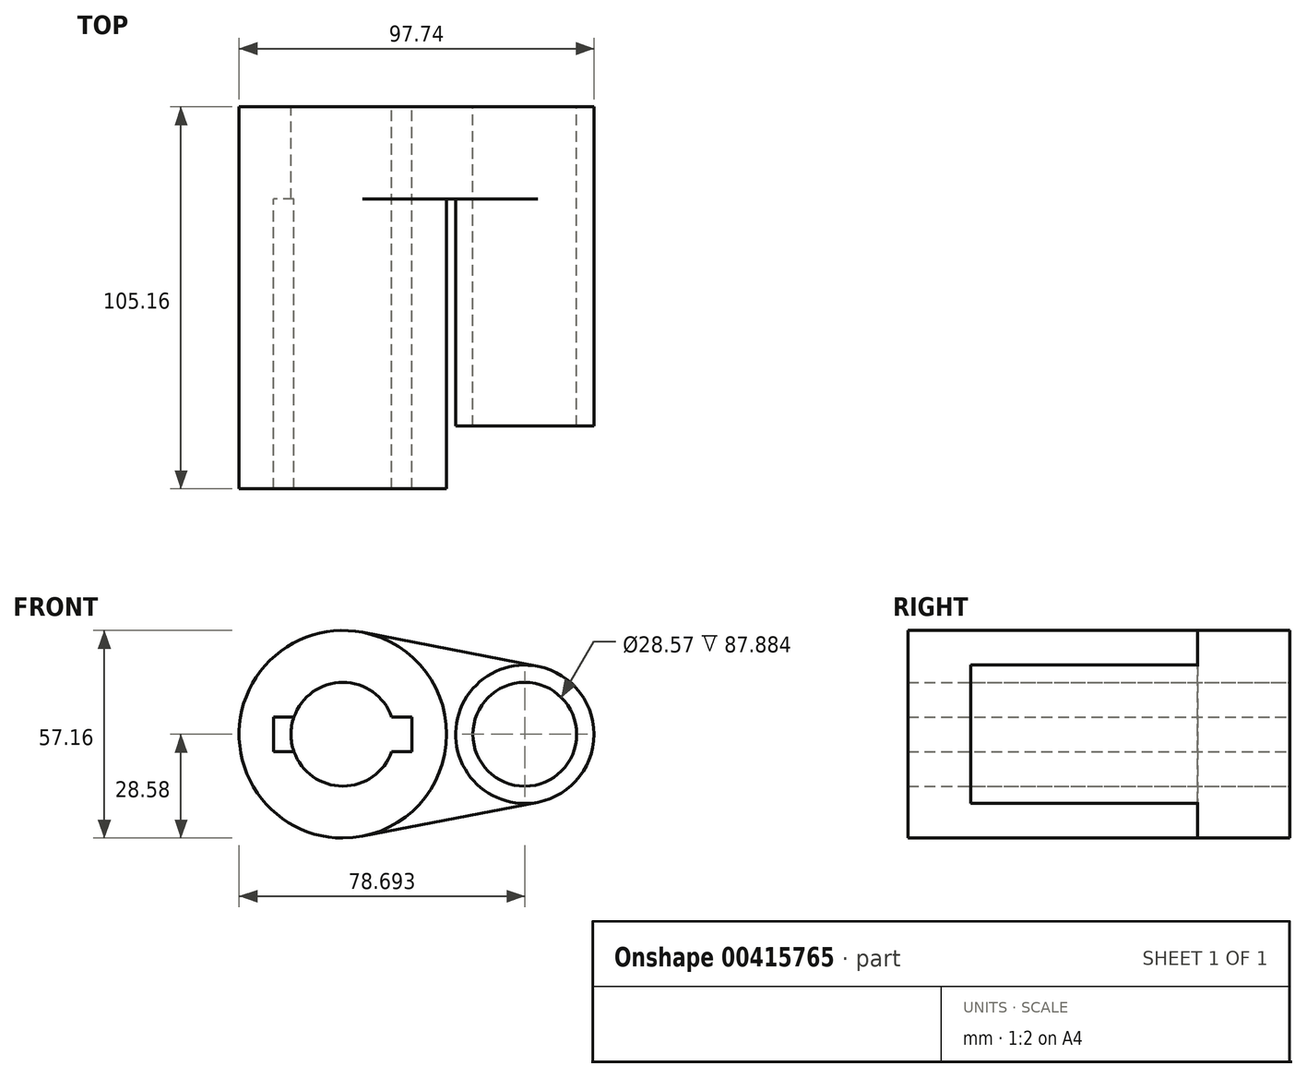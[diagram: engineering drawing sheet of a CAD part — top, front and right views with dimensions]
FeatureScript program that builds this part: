
annotation { "Feature Type Name" : "Feature", "Feature Type Description" : "" }
export const myFeature = defineFeature(function(context is Context, id is Id, definition is map)
    precondition{}
    {
        {
            var Q0;
            Q0=qCreatedBy(makeId("Front.planeOp"),FACE);
            var sketch = newSketch(context, id + "F0", { "sketchPlane" : qUnion([Q0])});
            skCircle(sketch, "E0", {"center": v(0, 0) * mm, "radius": 28.58 * mm});
            skCircle(sketch, "E1", {"center": v(50.11, 0) * mm, "radius": 19.05 * mm});
            skCircle(sketch, "E2", {"center": v(0, 0) * mm, "radius": 14.29 * mm});
            skCircle(sketch, "E3", {"center": v(50.11, 0) * mm, "radius": 14.29 * mm});
            skLineSegment(sketch, "E4.bottom", {"start": v(-19.05, 4.76) * mm, "end": v(19.05, 4.76) * mm});
            skLineSegment(sketch, "E4.top", {"start": v(-19.05, -4.76) * mm, "end": v(19.05, -4.76) * mm});
            skLineSegment(sketch, "E4.left", {"start": v(-19.05, 4.76) * mm, "end": v(-19.05, -4.76) * mm});
            skLineSegment(sketch, "E4.right", {"start": v(19.05, 4.76) * mm, "end": v(19.05, -4.76) * mm});
            skLineSegment(sketch, "E5", {"start": v(5.43, 28.05) * mm, "end": v(53.73, 18.7) * mm});
            skLineSegment(sketch, "E6", {"start": v(5.43, -28.05) * mm, "end": v(53.73, -18.7) * mm});
            skSolve(sketch);
        }
        {
            var Q0;
            {var subQ5=sQuery(id+"F0.wireOp",EDGE,"E4.left");Q0=makeQuery(id+"F0.imprint","IMPRINT",FACE,{"disambiguationData":[TD([[makeQuery(id+"F0.imprint","IMPRINT",EDGE,{"derivedFrom":subQ5}),1.0]])]});}
            var Q1;
            {var subQ4=sQuery(id+"F0.wireOp",EDGE,"E4.left");Q1=makeQuery(id+"F0.imprint","IMPRINT",FACE,{"disambiguationData":[TD([[makeQuery(id+"F0.imprint","IMPRINT",EDGE,{"derivedFrom":subQ4}),-1.0]])]});}
            var Q2;
            {var subQ0=sQuery(id+"F0.wireOp",EDGE,"E5");Q2=makeQuery(id+"F0.imprint","IMPRINT",FACE,{"disambiguationData":[TD([[makeQuery(id+"F0.imprint","IMPRINT",EDGE,{"derivedFrom":subQ0}),-1.0]])]});}
            var Q3;
            Q3=makeQuery(id+"F0.imprint","IMPRINT",FACE,{"disambiguationData":[TD([[makeQuery(id+"F0.imprint","IMPRINT",EDGE,{"derivedFrom":sQuery(id+"F0.wireOp",EDGE,"E3")}),-1.0]])]});
            extrude(context, id + "F1", {"entities" : qUnion([Q0, Q1, Q2, Q3]), "depth" : 25.4 * mm});
        }
        {
            var Q0;
            {var subQ4=sQuery(id+"F0.wireOp",EDGE,"E4.left");Q0=makeQuery(id+"F0.imprint","IMPRINT",FACE,{"disambiguationData":[TD([[makeQuery(id+"F0.imprint","IMPRINT",EDGE,{"derivedFrom":subQ4}),-1.0]])]});}
            extrude(context, id + "F2", {"entities" : qUnion([Q0]), "operationType" : NewBodyOperationType.ADD, "depth" : 105.16 * mm});
        }
        {
            var Q0;
            Q0=makeQuery(id+"F0.imprint","IMPRINT",FACE,{"disambiguationData":[TD([[makeQuery(id+"F0.imprint","IMPRINT",EDGE,{"derivedFrom":sQuery(id+"F0.wireOp",EDGE,"E3")}),-1.0]])]});
            extrude(context, id + "F3", {"entities" : qUnion([Q0]), "operationType" : NewBodyOperationType.ADD, "depth" : 87.88 * mm});
        }
    });
